# Revit family: P2E_2863-2862-2606_OS265
name_source: partatom
category: Porte
units: mm (PartAtom-declared; Revit-internal decimal feet)

## family parameters
Condiviso = No
Host = Muro
Numero OmniClass = 23.30.10.00
Punto di calcolo locali = No
Sempre verticale = Sì
Taglio con vuoti quando caricato = No
Titolo OmniClass = Doors

## types (4) — shared parameters
Chiusura muro = Per host
Costruzione analitica = <Nessuno>
Descrizione = Porta a due ante apertura esterna
Funzione = Interno
H_Max = 2900 mm
H_Min = 1600 mm  [stored 5.24934 ft]
H_maniglia = 1000 mm  [stored 3.28084 ft]
L_Max = 2000 mm  [stored 6.56168 ft]
L_Min = 800 mm  [stored 2.62467 ft]
Larghezza telaio = 75 mm
Modello = OS2 65
Produttore = Secco Sistemi Spa
Proiezione telaio est. = 25 mm  [stored 0.082021 ft]
Proiezione telaio int. = 25 mm  [stored 0.082021 ft]
URL = https://www.seccosistemi.com
WARNING = No
n2_cerniere = 2
n3_cerniere = 3
n4_cerniere = 4
nota tecnica = https://www.seccosistemi.com
numero_cerniere = 3
zero-valued in all types: H_A

## per-type parameters (varying)
| type | Altezza | Altezza_ante | H | H1 | H_vetro | L | L1 | L_A1 | L_A2 | L_v | L_vetro | Larghezza | Larghezza_1A | Larghezza_2A | MATERIALE |
| Acciaio zincato | 2500 mm  [stored 8.2021 ft] | 2500 mm  [stored 8.2021 ft] | 2500 mm  [stored 8.2021 ft] | 2500 mm  [stored 8.2021 ft] | 2424 mm | 1100 mm | 1100 mm | 566 mm | 566 mm | 490 mm | 490 mm | 1100 mm | 566 mm | 566 mm | Acciaio |
| Acciaio inox | 2500 mm  [stored 8.2021 ft] | 2500 mm  [stored 8.2021 ft] | 2500 mm  [stored 8.2021 ft] | 2500 mm  [stored 8.2021 ft] | 2424 mm | 1100 mm | 1100 mm | 566 mm | 566 mm | 490 mm | 490 mm | 1100 mm | 566 mm | 566 mm | Acciaio inox, spazzolato |
| Acciaio Corten | 2000 mm  [stored 6.56168 ft] | 2000 mm  [stored 6.56168 ft] | 2000 mm  [stored 6.56168 ft] | 2000 mm  [stored 6.56168 ft] | 1924 mm | 1200 mm  [stored 3.93701 ft] | 1200 mm  [stored 3.93701 ft] | 616 mm | 616 mm | 540 mm | 540 mm | 1200 mm  [stored 3.93701 ft] | 616 mm | 616 mm | Acciaio corten |
| Ottone | 2000 mm  [stored 6.56168 ft] | 2000 mm  [stored 6.56168 ft] | 2000 mm  [stored 6.56168 ft] | 2000 mm  [stored 6.56168 ft] | 1924 mm | 1500 mm | 1500 mm | 766 mm | 766 mm | 690 mm | 690 mm | 1500 mm | 766 mm | 766 mm | Ottone |

note: [stored X ft] marks values corroborated as IEEE doubles in the binary element streams (Revit-internal decimal feet)
